# Revit family: EKF_EE_БоковаяПанель(2шт)ВРУ-1UnitR_PROxima
name_source: partatom
category: Электрооборудование
units: mm (PartAtom-declared; Revit-internal decimal feet)

## family parameters
Всегда вертикально = Нет
На основе рабочей плоскости = Да
Общий = Да
При загрузке вырезать с полостями = Нет
Размер круглого соединителя = Использовать диаметр
Тип детали = Силовой щит
Точка расчета площади = Нет

## types (2) — shared parameters
ADSK_Единица измерения = шт.
ADSK_Завод-изготовитель = EKF
ADSK_Количество = 1
ADSK_Марка = Боковая панель
ADSK_Материал = RAL 7035_Сталь
ADSK_Обозначение = Боковая панель
ADSK_Размер_Глубина = 2 мм
ADSK_Размер_Ширина = 450 мм
Изготовитель = EKF
Серия номенклатуры = Unit PROxima
Степень защиты IP = -
ТВ = EKF_2
Тип установки = -
zero-valued in all types: ADSK_Масса, Отметка по умолчанию

## per-type parameters (varying)
| type | ADSK_Код изделия | ADSK_Размер_Высота | Тип |
| Боковая панель (2шт) для ВРУ-1 (1800хШх450) Unit R разборного EKF PROxima | mb09-03-01 | 1800 мм | 5 мм |
| Боковая панель (2шт) для ВРУ-1 (2000хШх450) Unit R разборного EKF PROxima | mb09-03-02 | 2000 мм | 6 мм |

note: column(s) folded — value = type name in every type: ADSK_Наименование
